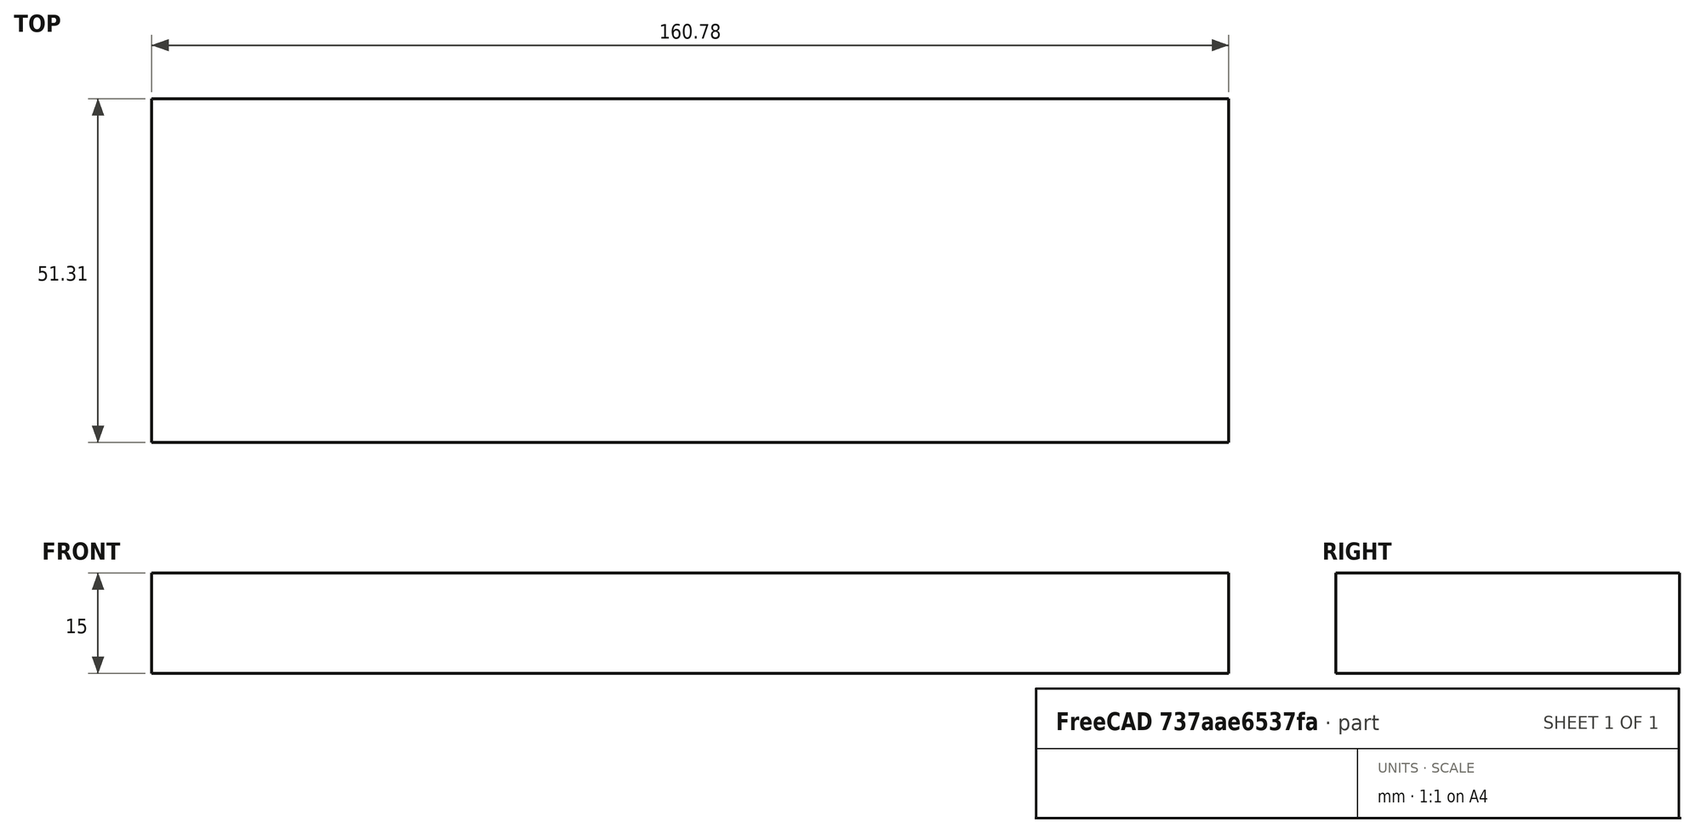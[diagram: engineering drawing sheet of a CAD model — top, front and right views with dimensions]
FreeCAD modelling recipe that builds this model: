
FCSTD DOCUMENT  (FreeCAD 0.21R33694 (Git))
Label: case
License: All rights reserved
LicenseURL: http://en.wikipedia.org/wiki/All_rights_reserved
objects: App::Part×1, Sketcher::SketchObject×1, PartDesign::Pad×1, PartDesign::Body×1, Spreadsheet::Sheet×1
note: 4 computed .brp shape members not serialized (recipe doc carries the construction recipe); baked Part::Feature solids carry a one-line shape summary decoded from their .brp

FEATURE [App::Part] Part  label="Case"
  Origin = -> Origin
FEATURE [Sketcher::SketchObject] Sketch
  FullyConstrained = true
  MapMode = 5
  Support = -> [XY_Plane001]
  expr: Constraints[8] = Spreadsheet.pcb_length
  expr: Constraints[9] = Spreadsheet.pcb_width
  sketch-geometry (4):
    g0: LineSegment StartX=0 StartY=51.308 StartZ=0 EndX=160.782 EndY=51.308 EndZ=0
    g1: LineSegment StartX=160.782 StartY=51.308 StartZ=0 EndX=160.782 EndY=0 EndZ=0
    g2: LineSegment StartX=160.782 StartY=0 StartZ=0 EndX=0 EndY=0 EndZ=0
    g3: LineSegment StartX=0 StartY=0 StartZ=0 EndX=0 EndY=51.308 EndZ=0
  constraints (11):
    c: Coincident(g0,g1)
    c: Coincident(g1,g2)
    c: Coincident(g2,g3)
    c: Coincident(g3,g0)
    c: Horizontal(g0)
    c: Horizontal(g2)
    c: Vertical(g1)
    c: Vertical(g3)
    c: DistanceX(g0,g0) = 160.782
    c: DistanceY(g1,g1) = 51.308
    c: Coincident(g-1,g2)
FEATURE [PartDesign::Pad] Pad
  Direction = (0,0,1)
  Length = 15
  Length2 = 10
  Profile = -> Sketch
  ReferenceAxis = -> Sketch [N_Axis]
  Type = 0
FEATURE [PartDesign::Body] Body  label="case"
  Group = -> [Sketch,Pad]
  Origin = -> Origin001
  Tip = -> Pad
FEATURE [Spreadsheet::Sheet] Spreadsheet
  cells = A1='pcb_width; B1(pcb_width)=51.308; A2='pcb_length; B2(pcb_length)=160.782; A3='wall_thickness; B3(wall_thickness)=0.5
